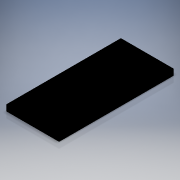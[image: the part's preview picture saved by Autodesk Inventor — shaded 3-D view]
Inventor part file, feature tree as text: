
AUTODESK INVENTOR PART (.ipt)
format: ipt  version: 2018 (Build 220112000, 112)  size: 134,656 bytes
history: native  units: in
note: dims shown in document units (in); Inventor stores cm internally (conversion verified against a paired STEP export)
features: extrude x3, sketch x3, fillet x2
ambient origin geometry x8: Origin, YZ Plane, XZ Plane, XY Plane, X Axis, Y Axis, Z Axis, Center Point
bodies: Solid1 (feature_tree)
feature tree (8):
  extrude  "Extrusion1"  Depth=21.69in
  extrude  "Extrusion2"  Depth=0.125in
  fillet  "Fillet1"  Radius=0.125in
  extrude  "Extrusion3"  Depth=20.0in
  fillet  "Fillet2"  Radius=4.0in
  sketch  "Sketch1"  dims[d0=47.08in d1=21.69in]
  sketch  "Sketch2"  dims[d2=0.5in d3=0.0in d4=0.125in d5=0.125in]
  sketch  "Sketch3"  dims[d6=2.0in d7=0.0in d8=20.0in d9=4.0in d10=1.9in d11=0.0in d12=2.0in]
